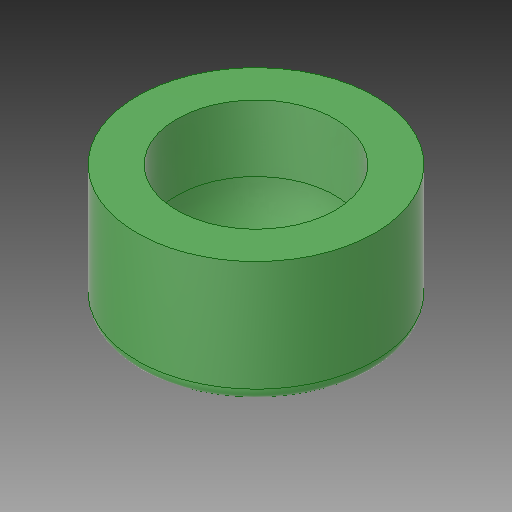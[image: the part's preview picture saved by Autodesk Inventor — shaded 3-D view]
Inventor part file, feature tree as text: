
AUTODESK INVENTOR PART (.ipt)
format: ipt  version: 2019.3 (Build 233278000, 278)  size: 148,992 bytes
history: native  units: mm
features: other x1, revolve x1, fillet x1, sketch x1
ambient origin geometry x8: Origin, YZ Plane, XZ Plane, XY Plane, X Axis, Y Axis, Z Axis, Center Point
bodies: Body1 (feature_tree)
feature tree (4):
  other  "Твердое тело1"
  revolve  "Вращение1"
  fillet  "Сопряжение1"  Radius=18.0mm
  sketch  "Эскиз1"
